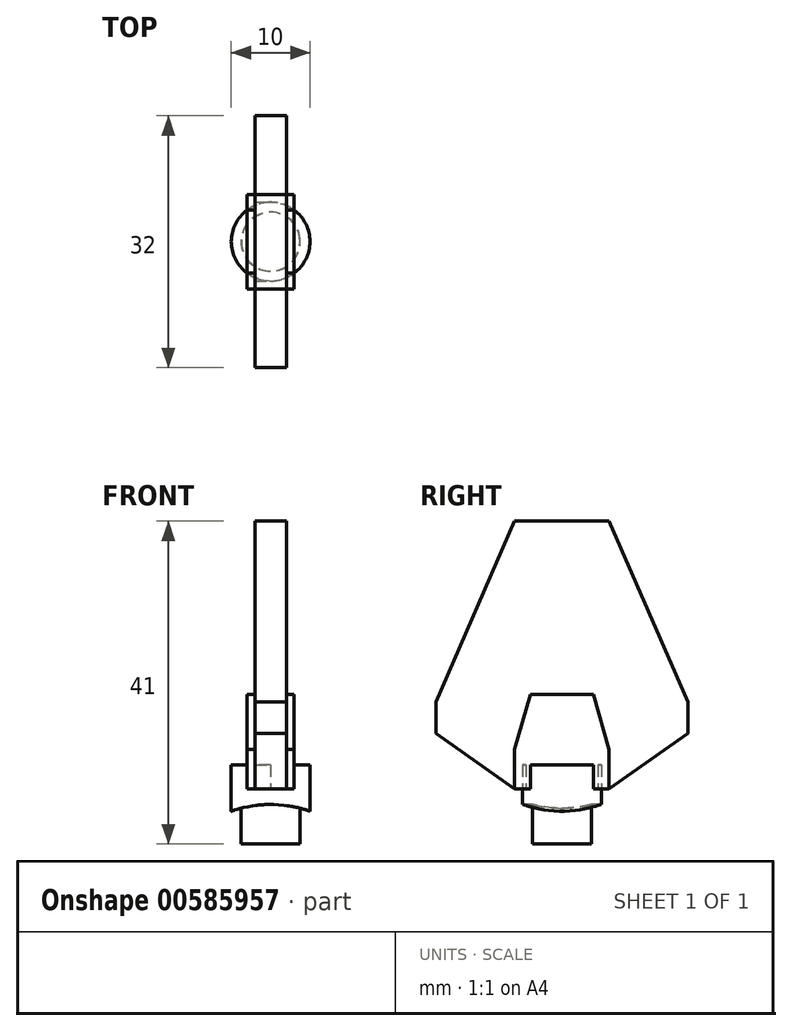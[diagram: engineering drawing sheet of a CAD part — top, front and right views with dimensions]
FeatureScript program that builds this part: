
annotation { "Feature Type Name" : "Feature", "Feature Type Description" : "" }
export const myFeature = defineFeature(function(context is Context, id is Id, definition is map)
    precondition{}
    {
        {
            var Q0;
            Q0=qCreatedBy(makeId("Top.planeOp"),FACE);
            var sketch = newSketch(context, id + "F0", { "sketchPlane" : qUnion([Q0])});
            skCircle(sketch, "E0", {"center": v(0, 0) * mm, "radius": 5 * mm});
            skSolve(sketch);
        }
        {
            var Q0;
            Q0 = qSketchRegion(id + "F0", true);
            extrude(context, id + "F1", {"entities" : qUnion([Q0]), "depth" : 6 * mm, "offsetDistance" : 25 * mm});
        }
        {
            var Q0;
            Q0=qCreatedBy(makeId("Front.planeOp"),FACE);
            cPlane(context, id + "F2", {"entities" : qUnion([Q0]), "cplaneType" : CPlaneType.OFFSET, "offset" : 6 * mm, "width" : 150 * mm, "height" : 150 * mm});
        }
        {
            var Q0;
            Q0=qCreatedBy(id+"F2.planeOp",FACE);
            var sketch = newSketch(context, id + "F3", { "sketchPlane" : qUnion([Q0])});
            skLineSegment(sketch, "E1", {"start": v(0, 0) * mm, "end": v(0, -14) * mm});
            skCircle(sketch, "E2", {"center": v(0, -14) * mm, "radius": 15 * mm});
            skSolve(sketch);
        }
        {
            var Q0;
            Q0=makeQuery(id+"F3.imprint","IMPRINT",FACE,{"disambiguationData":[TD([[makeQuery(id+"F3.imprint","IMPRINT",EDGE,{"derivedFrom":sQuery(id+"F3.wireOp",EDGE,"E2")}),1.0]])]});
            extrude(context, id + "F4", {"entities" : qUnion([Q0]), "operationType" : NewBodyOperationType.REMOVE, "oppositeDirection" : true, "depth" : 25 * mm, "offsetDistance" : 25 * mm});
        }
        {
            var Q0;
            Q0=makeQuery(id+"F1.opExtrude","CAP_FACE",FACE,{"disambiguationData":[OSD([sQuery(id+"F0.wireOp",EDGE,"E0")])],"isStart":false});
            var sketch = newSketch(context, id + "F5", { "sketchPlane" : qUnion([Q0])});
            skCircle(sketch, "E3", {"center": v(0, 0) * mm, "radius": 3.75 * mm});
            skSolve(sketch);
        }
        {
            var Q0;
            Q0 = qSketchRegion(id + "F5", true);
            extrude(context, id + "F6", {"entities" : qUnion([Q0]), "operationType" : NewBodyOperationType.ADD, "oppositeDirection" : true, "depth" : 10 * mm, "offsetDistance" : 25 * mm});
        }
        {
            var Q0;
            Q0=qCreatedBy(makeId("Right.planeOp"),FACE);
            var sketch = newSketch(context, id + "F7", { "sketchPlane" : qUnion([Q0])});
            skLineSegment(sketch, "E4", {"start": v(0, 0) * mm, "end": v(0, 20) * mm});
            skLineSegment(sketch, "E5.bottom", {"start": v(16, 37) * mm, "end": v(-16, 37) * mm});
            skLineSegment(sketch, "E5.top", {"start": v(16, 3) * mm, "end": v(-16, 3) * mm});
            skLineSegment(sketch, "E5.left", {"start": v(16, 37) * mm, "end": v(16, 3) * mm});
            skLineSegment(sketch, "E5.right", {"start": v(-16, 37) * mm, "end": v(-16, 3) * mm});
            skPoint(sketch, "E5.middle", {"position": v(0, 20) * mm});
            skSolve(sketch);
        }
        {
            var Q0;
            Q0=makeQuery(id+"F7.imprint","IMPRINT",FACE,{"disambiguationData":[TD([[makeQuery(id+"F7.imprint","IMPRINT",EDGE,{"derivedFrom":sQuery(id+"F7.wireOp",EDGE,"E5.bottom")}),1.0]])]});
            extrude(context, id + "F8", {"entities" : qUnion([Q0]), "operationType" : NewBodyOperationType.ADD, "depth" : 2 * mm, "offsetDistance" : 25 * mm});
        }
        {
            var Q0;
            Q0=makeQuery(id+"F8.opExtrude","CAP_FACE",FACE,{"disambiguationData":[OSD([sQuery(id+"F7.wireOp",EDGE,"E5.bottom"),sQuery(id+"F7.wireOp",EDGE,"E5.top"),sQuery(id+"F7.wireOp",EDGE,"E5.left"),sQuery(id+"F7.wireOp",EDGE,"E5.right")])],"isStart":true});
            extrude(context, id + "F9", {"entities" : qUnion([Q0]), "operationType" : NewBodyOperationType.ADD, "depth" : 2 * mm, "offsetDistance" : 25 * mm});
        }
        {
            var Q0;
            {var subQ0=sQuery(id+"F7.wireOp",EDGE,"E5.right");var subQ1=sQuery(id+"F7.wireOp",EDGE,"E5.top");Q0=makeQuery(id+"F9.boolean.opBoolean","MERGE",EDGE,{"derivedFrom":[makeQuery(id+"F8.opExtrude","SWEPT_EDGE",EDGE,{"disambiguationData":[OSD([subQ1,subQ0])]}),makeQuery(id+"F9.opExtrude","SWEPT_EDGE",EDGE,{"disambiguationData":[OSD([subQ1,subQ0])]})]});}
            chamfer(context, id + "F10", {"entities" : qUnion([Q0]), "chamferType" : ChamferType.TWO_OFFSETS, "width1" : 10 * mm, "oppositeDirection" : false, "width2" : 7 * mm, "tangentPropagation" : true});
        }
        {
            var Q0;
            {var subQ0=sQuery(id+"F7.wireOp",EDGE,"E5.left");var subQ1=sQuery(id+"F7.wireOp",EDGE,"E5.top");Q0=makeQuery(id+"F9.boolean.opBoolean","MERGE",EDGE,{"derivedFrom":[makeQuery(id+"F8.opExtrude","SWEPT_EDGE",EDGE,{"disambiguationData":[OSD([subQ1,subQ0])]}),makeQuery(id+"F9.opExtrude","SWEPT_EDGE",EDGE,{"disambiguationData":[OSD([subQ1,subQ0])]})]});}
            chamfer(context, id + "F11", {"entities" : qUnion([Q0]), "chamferType" : ChamferType.TWO_OFFSETS, "width1" : 7 * mm, "oppositeDirection" : false, "width2" : 10 * mm, "tangentPropagation" : true});
        }
        {
            var Q0;
            {var subQ0=sQuery(id+"F7.wireOp",EDGE,"E5.right");var subQ1=sQuery(id+"F7.wireOp",EDGE,"E5.bottom");Q0=makeQuery(id+"F9.boolean.opBoolean","MERGE",EDGE,{"derivedFrom":[makeQuery(id+"F8.opExtrude","SWEPT_EDGE",EDGE,{"disambiguationData":[OSD([subQ1,subQ0])]}),makeQuery(id+"F9.opExtrude","SWEPT_EDGE",EDGE,{"disambiguationData":[OSD([subQ1,subQ0])]})]});}
            chamfer(context, id + "F12", {"entities" : qUnion([Q0]), "chamferType" : ChamferType.TWO_OFFSETS, "width1" : 23 * mm, "oppositeDirection" : false, "width2" : 10 * mm, "tangentPropagation" : true});
        }
        {
            var Q0;
            {var subQ0=sQuery(id+"F7.wireOp",EDGE,"E5.left");var subQ1=sQuery(id+"F7.wireOp",EDGE,"E5.bottom");Q0=makeQuery(id+"F9.boolean.opBoolean","MERGE",EDGE,{"derivedFrom":[makeQuery(id+"F8.opExtrude","SWEPT_EDGE",EDGE,{"disambiguationData":[OSD([subQ1,subQ0])]}),makeQuery(id+"F9.opExtrude","SWEPT_EDGE",EDGE,{"disambiguationData":[OSD([subQ1,subQ0])]})]});}
            chamfer(context, id + "F13", {"entities" : qUnion([Q0]), "chamferType" : ChamferType.TWO_OFFSETS, "width1" : 10 * mm, "oppositeDirection" : false, "width2" : 23 * mm, "tangentPropagation" : true});
        }
        {
            var Q0;
            Q0=makeQuery(id+"F9.opExtrude","CAP_FACE",FACE,{"disambiguationData":[OSD([sQuery(id+"F7.wireOp",EDGE,"E5.bottom"),sQuery(id+"F7.wireOp",EDGE,"E5.top"),sQuery(id+"F7.wireOp",EDGE,"E5.left"),sQuery(id+"F7.wireOp",EDGE,"E5.right")])],"isStart":false});
            var sketch = newSketch(context, id + "F14", { "sketchPlane" : qUnion([Q0])});
            skLineSegment(sketch, "E6.bottom", {"start": v(-6, 3) * mm, "end": v(6, 3) * mm});
            skLineSegment(sketch, "E6.top", {"start": v(-6, 15) * mm, "end": v(6, 15) * mm});
            skLineSegment(sketch, "E6.left", {"start": v(-6, 3) * mm, "end": v(-6, 15) * mm});
            skLineSegment(sketch, "E6.right", {"start": v(6, 3) * mm, "end": v(6, 15) * mm});
            skSolve(sketch);
        }
        {
            var Q0;
            Q0 = qSketchRegion(id + "F14", true);
            extrude(context, id + "F15", {"entities" : qUnion([Q0]), "operationType" : NewBodyOperationType.ADD, "depth" : 1 * mm, "offsetDistance" : 25 * mm});
        }
        {
            var Q0;
            Q0=makeQuery(id+"F8.opExtrude","CAP_FACE",FACE,{"disambiguationData":[OSD([sQuery(id+"F7.wireOp",EDGE,"E5.bottom"),sQuery(id+"F7.wireOp",EDGE,"E5.top"),sQuery(id+"F7.wireOp",EDGE,"E5.left"),sQuery(id+"F7.wireOp",EDGE,"E5.right")])],"isStart":false});
            var sketch = newSketch(context, id + "F16", { "sketchPlane" : qUnion([Q0])});
            skLineSegment(sketch, "E7.bottom", {"start": v(-6, 3) * mm, "end": v(6, 3) * mm});
            skLineSegment(sketch, "E7.top", {"start": v(-6, 15) * mm, "end": v(6, 15) * mm});
            skLineSegment(sketch, "E7.left", {"start": v(-6, 3) * mm, "end": v(-6, 15) * mm});
            skLineSegment(sketch, "E7.right", {"start": v(6, 3) * mm, "end": v(6, 15) * mm});
            skSolve(sketch);
        }
        {
            var Q0;
            Q0 = qSketchRegion(id + "F16", true);
            extrude(context, id + "F17", {"entities" : qUnion([Q0]), "operationType" : NewBodyOperationType.ADD, "depth" : 1 * mm, "offsetDistance" : 25 * mm});
        }
        {
            var Q0;
            Q0=makeQuery(id+"F15.opExtrude","SWEPT_EDGE",EDGE,{"disambiguationData":[OSD([sQuery(id+"F14.wireOp",EDGE,"E6.top"),sQuery(id+"F14.wireOp",EDGE,"E6.right")])]});
            var Q1;
            Q1=makeQuery(id+"F15.opExtrude","SWEPT_EDGE",EDGE,{"disambiguationData":[OSD([sQuery(id+"F14.wireOp",EDGE,"E6.top"),sQuery(id+"F14.wireOp",EDGE,"E6.left")])]});
            chamfer(context, id + "F18", {"entities" : qUnion([Q0, Q1]), "chamferType" : ChamferType.TWO_OFFSETS, "width1" : 2 * mm, "oppositeDirection" : false, "width2" : 7 * mm, "tangentPropagation" : true});
        }
        {
            var Q0;
            Q0=makeQuery(id+"F17.opExtrude","SWEPT_EDGE",EDGE,{"disambiguationData":[OSD([sQuery(id+"F16.wireOp",EDGE,"E7.top"),sQuery(id+"F16.wireOp",EDGE,"E7.right")])]});
            var Q1;
            Q1=makeQuery(id+"F17.opExtrude","SWEPT_EDGE",EDGE,{"disambiguationData":[OSD([sQuery(id+"F16.wireOp",EDGE,"E7.top"),sQuery(id+"F16.wireOp",EDGE,"E7.left")])]});
            chamfer(context, id + "F19", {"entities" : qUnion([Q0, Q1]), "chamferType" : ChamferType.TWO_OFFSETS, "width1" : 2 * mm, "oppositeDirection" : false, "width2" : 7 * mm, "tangentPropagation" : true});
        }
    });
